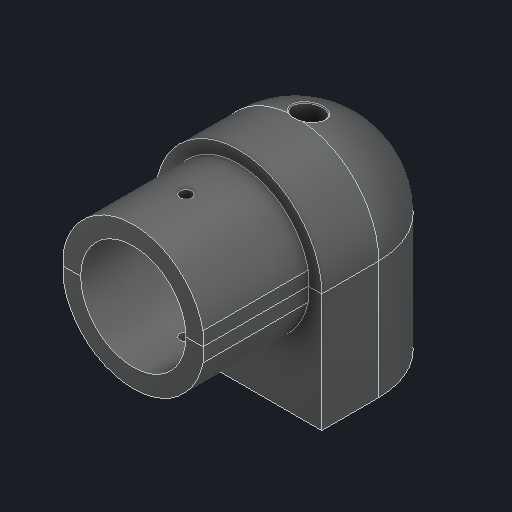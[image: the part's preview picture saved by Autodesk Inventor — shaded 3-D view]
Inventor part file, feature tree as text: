
AUTODESK INVENTOR PART (.ipt)
format: ipt  version: 2024 (Build 280153000, 153)  size: 212,992 bytes
history: native  units: in
note: dims shown in document units (in); Inventor stores cm internally (conversion verified against a paired STEP export)
features: fillet x1
ambient origin geometry x8: Origin, YZ Plane, XZ Plane, XY Plane, X Axis, Y Axis, Z Axis, Center Point
bodies: Solid1 (feature_tree)
feature tree (1):
  fillet  "Fillet5"  [1 undecoded]
note: 1 required parameter value undecoded (feature->parameter linkage not recoverable at this tier; creation-order binding heuristic only, values carry confidence <= 0.55)
